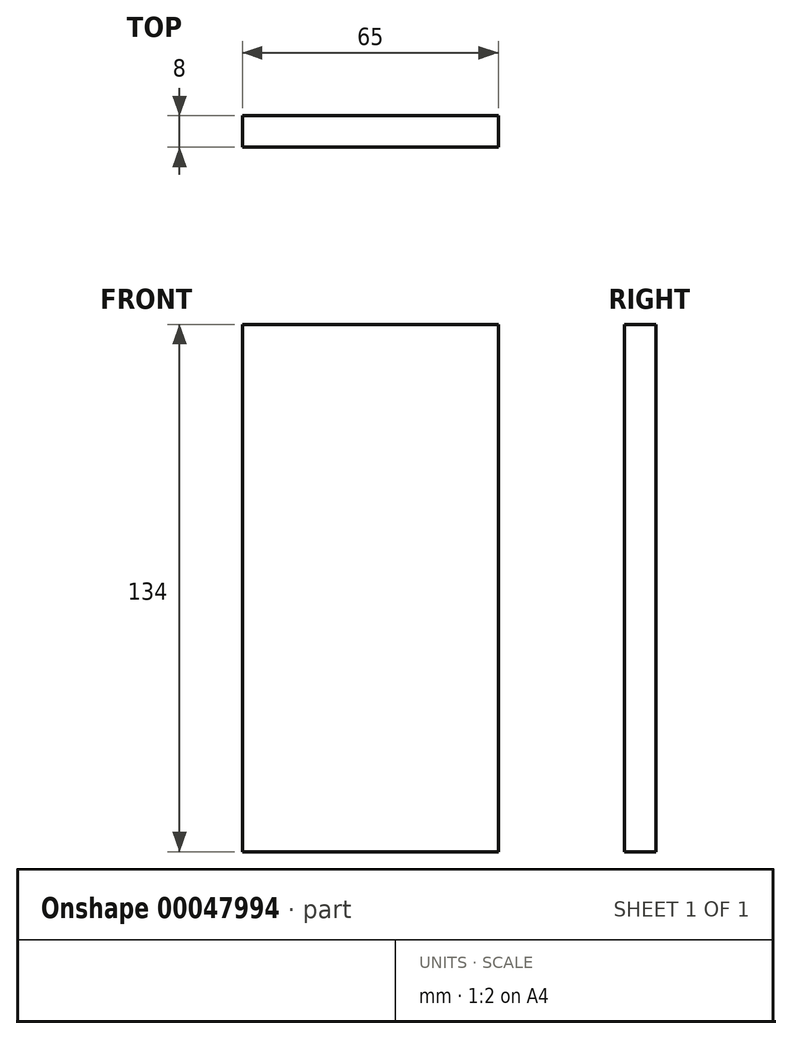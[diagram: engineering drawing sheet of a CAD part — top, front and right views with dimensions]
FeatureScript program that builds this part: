
annotation { "Feature Type Name" : "Feature", "Feature Type Description" : "" }
export const myFeature = defineFeature(function(context is Context, id is Id, definition is map)
    precondition{}
    {
        {
            var Q0;
            Q0=qCreatedBy(makeId("Top.planeOp"),FACE);
            var sketch = newSketch(context, id + "F0", { "sketchPlane" : qUnion([Q0])});
            skLineSegment(sketch, "E0.bottom", {"start": v(28.5, 4) * mm, "end": v(-36.5, 4) * mm});
            skLineSegment(sketch, "E0.top", {"start": v(28.5, -4) * mm, "end": v(-36.5, -4) * mm});
            skLineSegment(sketch, "E0.left", {"start": v(28.5, 4) * mm, "end": v(28.5, -4) * mm});
            skLineSegment(sketch, "E0.right", {"start": v(-36.5, 4) * mm, "end": v(-36.5, -4) * mm});
            skSolve(sketch);
        }
        {
            var Q0;
            Q0 = qSketchRegion(id + "F0", true);
            extrude(context, id + "F1", {"entities" : qUnion([Q0]), "depth" : (150 - 2 * 8) * mm});
        }
    });
